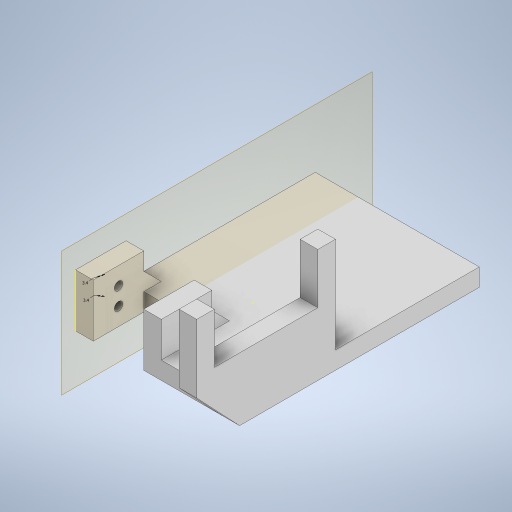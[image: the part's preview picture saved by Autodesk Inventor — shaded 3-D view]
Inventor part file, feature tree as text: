
AUTODESK INVENTOR PART (.ipt)
format: ipt  version: 2024 (Build 280153020, 153B)  size: 346,112 bytes
history: native  units: in
note: dims shown in document units (in); Inventor stores cm internally (conversion verified against a paired STEP export)
features: sketch x14, extrude x10, mirror x2, plane x1
ambient origin geometry x8: Origin, YZ Plane, XZ Plane, XY Plane, X Axis, Y Axis, Z Axis, Center Point
bodies: Solid1 (feature_tree)
feature tree (27):
  extrude  "Extrusion1"  Depth=2.9528in
  extrude  "Extrusion4"  Depth=0.2756in
  extrude  "Extrusion5"  Depth=0.7874in
  extrude  "Extrusion6"  TaperAngle=90.0deg  [1 undecoded]
  extrude  "Extrusion7"  Depth=0.5512in TaperAngle=0.0deg
  extrude  "Extrusion8"  Depth=1.4961in
  extrude  "Extrusion9"  Depth=0.2756in
  extrude  "Extrusion10"  Depth=2.1654in
  sketch  "Sketch14"  dims[d30=0.2756in d31=0.2756in]
  sketch  "Sketch15"  dims[d32=0.7874in d33=0.0in d34=1.3376in d35=0.0in]
  sketch  "Sketch16"  dims[d37=0.2756in]
  plane  "Work Plane1"
  mirror  "Mirror1"
  extrude  "Extrusion12"  Depth=0.2756in
  mirror  "Mirror2"
  sketch  "Sketch19"  dims[d43=0.2756in]
  extrude  "Extrusion13"  Depth=0.7874in TaperAngle=0.0deg
  sketch  "Sketch1"  dims[d0=2.5591in d1=2.9528in]
  sketch  "Sketch6"  dims[d2=0.2756in d3=0.0in d13=0.2756in]
  sketch  "Sketch7"  dims[d14=0.7874in d15=0.7874in]
  sketch  "Sketch8"  dims[d16=0.7874in d17=90.0deg]
  sketch  "Sketch9"  dims[d18=0.5512in d19=0.0in d20=0.5512in d21=0.0in]
  sketch  "Sketch10"  dims[d22=0.2756in d23=1.4961in]
  sketch  "Sketch11"  dims[d24=0.7087in d25=0.0in d26=0.2756in]
  sketch  "Sketch13"  dims[d27=0.7874in d28=0.0in d29=2.1654in]
  sketch  "Sketch18"  dims[d38=0.7874in d39=0.0in]
  sketch  "Sketch20"  dims[d44=90.0deg d45=45.0deg d46=1.7874in d47=0.0in d52=0.1339in d53=0.1339in d54=0.1339in d55=0.1339in d56=0.3937in d57=0.0in d58=0.0197in d59=0.0344in]
note: 1 required parameter value undecoded (feature->parameter linkage not recoverable at this tier; creation-order binding heuristic only, values carry confidence <= 0.55)
